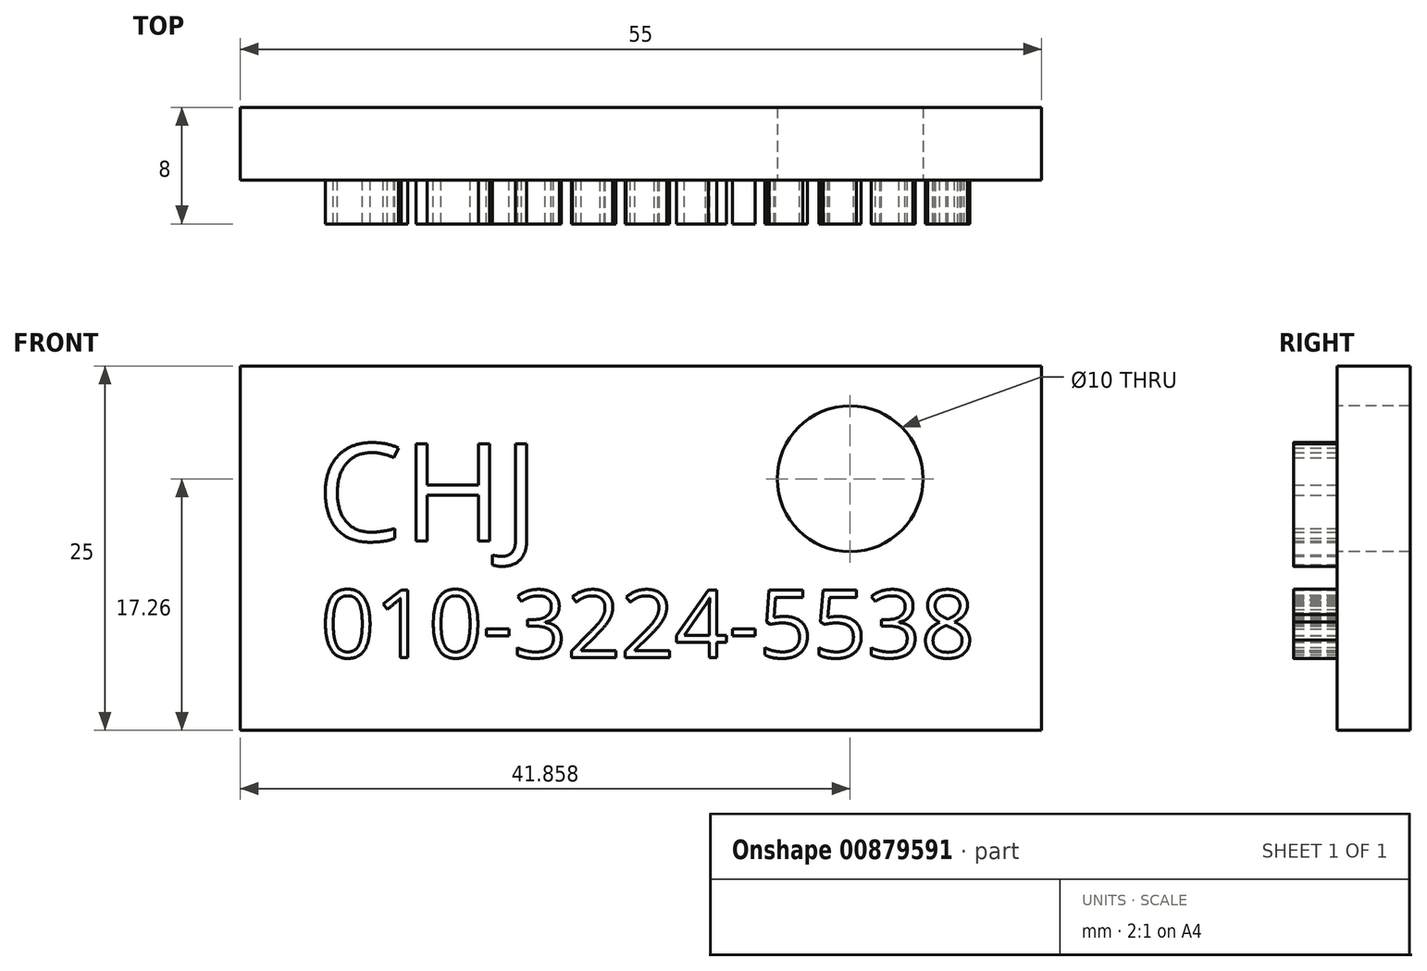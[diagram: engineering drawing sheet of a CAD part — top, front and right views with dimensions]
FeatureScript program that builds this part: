
annotation { "Feature Type Name" : "Feature", "Feature Type Description" : "" }
export const myFeature = defineFeature(function(context is Context, id is Id, definition is map)
    precondition{}
    {
        {
            var Q0;
            Q0=qCreatedBy(makeId("Front.planeOp"),FACE);
            var sketch = newSketch(context, id + "F0", { "sketchPlane" : qUnion([Q0])});
            skLineSegment(sketch, "E0.bottom", {"start": v(0, 0) * mm, "end": v(55, 0) * mm});
            skLineSegment(sketch, "E0.top", {"start": v(0, 25) * mm, "end": v(55, 25) * mm});
            skLineSegment(sketch, "E0.left", {"start": v(0, 0) * mm, "end": v(0, 25) * mm});
            skLineSegment(sketch, "E0.right", {"start": v(55, 0) * mm, "end": v(55, 25) * mm});
            skSolve(sketch);
        }
        {
            var Q0;
            Q0=makeQuery(id+"F0.imprint","IMPRINT",FACE,{"disambiguationData":[TD([[makeQuery(id+"F0.imprint","IMPRINT",EDGE,{"derivedFrom":sQuery(id+"F0.wireOp",EDGE,"E0.bottom")}),1.0]])]});
            extrude(context, id + "F1", {"entities" : qUnion([Q0]), "depth" : 5 * mm, "offsetDistance" : 25 * mm});
        }
        {
            var Q0;
            Q0=makeQuery(id+"F1.opExtrude","CAP_FACE",FACE,{"disambiguationData":[OSD([sQuery(id+"F0.wireOp",EDGE,"E0.bottom"),sQuery(id+"F0.wireOp",EDGE,"E0.top"),sQuery(id+"F0.wireOp",EDGE,"E0.left"),sQuery(id+"F0.wireOp",EDGE,"E0.right")])],"isStart":false});
            var sketch = newSketch(context, id + "F2", { "sketchPlane" : qUnion([Q0])});
            skText(sketch, "E1", { "text": "CHJ", "fontName": "OpenSans-Regular.ttf"});
            skText(sketch, "E2", { "text": "010-3224-5538", "fontName": "OpenSans-Regular.ttf"});
            const initialGuessF2  = {"E1": [0.00527, 0.013, 1, 0, 0.00671], "E2": [0.00553, 0.00499, 1, 0, 0.00466]};
            skSetInitialGuess(sketch, initialGuessF2);
            skSolve(sketch);
        }
        {
            var Q0;
            Q0=qSketchRegion(id+"F2",true);
            extrude(context, id + "F3", {"entities" : qUnion([Q0]), "operationType" : NewBodyOperationType.ADD, "depth" : 3 * mm, "offsetDistance" : 25 * mm});
        }
        {
            var Q0;
            {var subQ0=sQuery(id+"F0.wireOp",EDGE,"E0.left");var subQ1=sQuery(id+"F0.wireOp",EDGE,"E0.bottom");var subQ2=sQuery(id+"F0.wireOp",EDGE,"E0.right");var subQ3=sQuery(id+"F0.wireOp",EDGE,"E0.top");Q0=makeQuery(id+"F3.boolean.opBoolean","SPLIT",FACE,{"disambiguationData":[TD([makeQuery(id+"F1.opExtrude","SWEPT_FACE",FACE,{"disambiguationData":[OSD([subQ1])]})])],"derivedFrom":makeQuery(id+"F1.opExtrude","CAP_FACE",FACE,{"disambiguationData":[OSD([subQ1,subQ3,subQ0,subQ2])],"isStart":false})});}
            var sketch = newSketch(context, id + "F4", { "sketchPlane" : qUnion([Q0])});
            skCircle(sketch, "E3", {"center": v(41.86, 17.26) * mm, "radius": 5 * mm});
            skSolve(sketch);
        }
        {
            var Q0;
            Q0=makeQuery(id+"F4.imprint","IMPRINT",FACE,{"disambiguationData":[TD([[makeQuery(id+"F4.imprint","IMPRINT",EDGE,{"derivedFrom":sQuery(id+"F4.wireOp",EDGE,"E3")}),1.0]])]});
            var Q1;
            Q1=sQuery(id+"F4.wireOp",EDGE,"E3");
            extrude(context, id + "F5", {"entities" : qUnion([Q0]), "operationType" : NewBodyOperationType.REMOVE, "surfaceEntities" : qUnion([Q1]), "oppositeDirection" : true, "depth" : 25 * mm, "offsetDistance" : 25 * mm});
        }
    });
